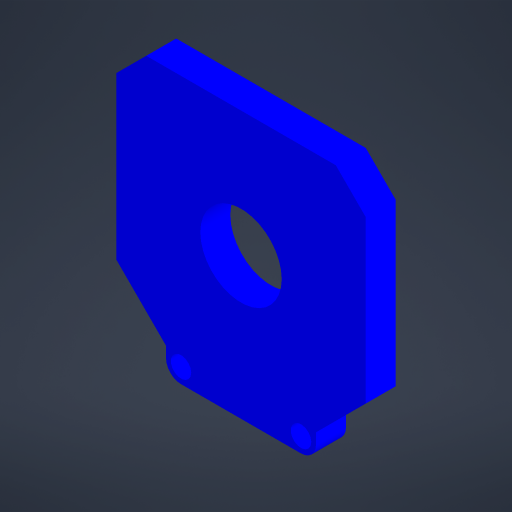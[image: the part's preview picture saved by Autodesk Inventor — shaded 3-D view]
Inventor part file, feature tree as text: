
AUTODESK INVENTOR PART (.ipt)
format: ipt  version: 2023.4 (Build 274418000, 418)  size: 203,264 bytes
history: native  units: mm
features: other x3, extrude x1, reference x1
ambient origin geometry x8: Origin, YZ Plane, XZ Plane, XY Plane, X Axis, Y Axis, Z Axis, Center Point
bodies: Solid1 (feature_tree)
feature tree (5):
  extrude  "Extrusion1"  Depth=5.0mm
  reference  "Reference2"
  other  "<path>\Projects\Project Protocube\Protocube\CAD, STL, OBJ Files\1 CAD\Cube 1x1 V5.iam"
  other  "Cube 1x1 V5.iam"
  other  "Cube 1x1 Bottom V5 Closed Slotted:1"
note: 1 file-system path scrubbed to <path> (originals preserved in map.json)
